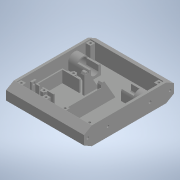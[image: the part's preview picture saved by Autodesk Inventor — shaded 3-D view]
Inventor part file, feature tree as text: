
AUTODESK INVENTOR PART (.ipt)
format: ipt  version: 2020 (Build 240168000, 168)  size: 610,816 bytes
history: native  units: in
note: dims shown in document units (in); Inventor stores cm internally (conversion verified against a paired STEP export)
features: extrude x18, sketch x17, projected_geometry x14, mirror x6, plane x1
ambient origin geometry x8: Origin, YZ Plane, XZ Plane, XY Plane, X Axis, Y Axis, Z Axis, Center Point
bodies: Solid1 (feature_tree)
feature tree (56):
  extrude  "Extrusion1"  Depth=5.9055in
  extrude  "Extrusion2"  TaperAngle=0.0deg  [1 undecoded]
  extrude  "Extrusion3"  Depth=1.063in
  extrude  "Extrusion4"  Depth=0.315in
  extrude  "Extrusion5"  TaperAngle=0.0deg  [1 undecoded]
  extrude  "Extrusion6"  Depth=0.5906in
  mirror  "Mirror1"
  extrude  "Extrusion7"  Depth=0.0787in
  mirror  "Mirror2"
  extrude  "Extrusion8"  Depth=0.6102in
  mirror  "Mirror3"
  plane  "Work Plane1"
  extrude  "Extrusion9"  Depth=0.7874in TaperAngle=0.0deg
  mirror  "Mirror4"
  extrude  "Extrusion10"  Depth=0.1654in TaperAngle=0.0deg
  extrude  "Extrusion11"  Depth=0.1575in
  extrude  "Extrusion12"  TaperAngle=0.0deg  [1 undecoded]
  extrude  "Extrusion13"  Depth=0.2756in
  extrude  "Extrusion14"  Depth=0.4331in
  extrude  "Extrusion17"  Depth=2.7559in
  extrude  "Extrusion18"  Depth=0.0413in
  mirror  "Mirror6"
  extrude  "Extrusion19"  TaperAngle=0.0deg  [1 undecoded]
  mirror  "Mirror7"
  extrude  "Extrusion20"  TaperAngle=60.0deg  [1 undecoded]
  sketch  "Sketch1"  dims[d0=1.1811in d1=5.9055in]
  sketch  "Sketch2"  dims[d2=5.1181in d3=0.0in]
  projected_geometry  "Projected Loop1"
  sketch  "Sketch3"  dims[d4=0.1575in d5=1.063in]
  projected_geometry  "Projected Loop2"
  projected_geometry  "Projected Loop3"
  sketch  "Sketch4"  dims[d6=0.0in d8=0.315in]
  projected_geometry  "Projected Loop4"
  sketch  "Sketch6"  dims[d10=0.993in d11=0.0in]
  sketch  "Sketch7"  dims[d12=0.6496in d13=0.5906in]
  sketch  "Sketch9"  dims[d14=1.5748in d15=0.0787in]
  sketch  "Sketch10"  dims[d16=0.5512in d17=0.0in d18=0.6102in]
  sketch  "Sketch12"  dims[d19=0.4803in d20=0.7874in d21=0.0in]
  projected_geometry  "Projected Loop6"
  projected_geometry  "Projected Loop7"
  projected_geometry  "Projected Loop8"
  sketch  "Sketch13"  dims[d22=0.1654in d23=6.063in d24=0.0in]
  sketch  "Sketch14"  dims[d25=0.5114in d26=0.1575in]
  sketch  "Sketch15"  dims[d27=1.5748in d28=0.0in d29=0.0in]
  projected_geometry  "Projected Loop15"
  sketch  "Sketch16"  dims[d30=0.1575in d31=0.2756in]
  projected_geometry  "Projected Loop19"
  projected_geometry  "Projected Loop20"
  projected_geometry  "Projected Loop21"
  projected_geometry  "Projected Loop22"
  projected_geometry  "Projected Loop23"
  projected_geometry  "Projected Loop24"
  sketch  "Sketch20"  dims[d32=0.0in d33=0.4331in]
  sketch  "Sketch21"  dims[d34=0.0827in d38=2.7559in]
  sketch  "Sketch22"  dims[d40=0.0413in d41=0.0909in]
  sketch  "Sketch23"  dims[d42=0.2362in d43=0.0in d44=60.0deg d45=0.0787in d46=0.315in d48=0.993in d49=0.0in d53=0.2756in d54=0.0in d55=0.4724in d56=1.2008in d57=1.6142in d58=1.5945in d59=0.0787in d60=0.0787in d62=0.315in d63=0.7677in d64=0.0in d66=0.1476in d67=0.2756in d68=0.0in d69=0.7874in d70=0.2953in d71=0.1181in d72=0.0in d89=0.0157in d90=0.0157in d91=0.1476in d92=0.1476in d96=0.315in d97=0.1575in d98=0.1181in d99=0.0in d102=0.1772in d104=0.3346in d105=135.0deg d106=0.2362in d107=0.0in d108=0.0394in d109=0.0in d110=0.0315in d111=0.0394in d112=0.0in]
note: 5 required parameter values undecoded (feature->parameter linkage not recoverable at this tier; creation-order binding heuristic only, values carry confidence <= 0.55)
